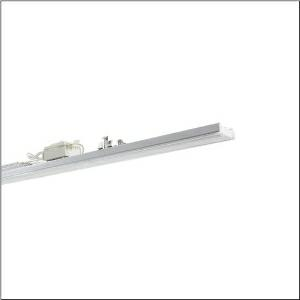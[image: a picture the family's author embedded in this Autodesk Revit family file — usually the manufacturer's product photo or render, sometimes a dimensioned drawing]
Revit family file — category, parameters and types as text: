
# Revit family: licross_r__21_recessed_mo_52tl12dv4fxg_13e3
name_source: partatom
category: Lighting Fixtures
units: mm (PartAtom-declared; Revit-internal decimal feet)

## family parameters
Cut with Voids When Loaded = No
Host = Face
Light Source = No
Part Type = Normal
Room Calculation Point = No
Round Connector Dimension = Use Diameter
Shared = No

## types (1)
- --- (1 x LED, 15420 lm, 85.3 W, 4000K)
    Apparent Load = 85 VA
    CIE Flux Codes = 72 92 99 100 100
    Color Rendering = 80
    Color Temperature = 4000K
    Default Elevation = 1800 mm
    Description = Licross® 21 Recessed MO, luminaire insert, of sheet steel, galvanised, coil coated, white, length: 2.250mm, width: 66mm, height: 67mm, LED rated luminous flux: 15.420lm, light colour: 840, control gear: DALI 2, with plug, 5-pole, with phase selection, mains connection: 220..240V, AC, 50/60Hz, rated input power: 85W, halogen-free wiring, primary optical cover: cover, of PMMA, light emission: direct distribution, primary light characteristic: symmetric, protection rating (complete): IP40, insulation class (complete): insulation class I (protective earthing), certification: CE, ENEC, VDE, UKCA, protection symbol: D if used in an environment without relevant dust loads with corresponding accessories, impact resistance: IK06, permissible ambient temperature for indoor applications: -25..+35°C, corresponds to IFS (International Featured Standards) requirements for safety and quality in the food industry, reducing of maximum allowable ambient temperature of 5°C with ceiling mounting, LABS conformity tested according to VDMA 24364:2018-05, packaging unit: 1 piece
    Height = 58 mm
    Lamp = 1 x LED
    Lamp Light Flux = 15420 lm
    Lamp Power = 85.3 W
    Lamp count = 1
    Length = 2250 mm
    Luminous efficacy = 181 lm/W
    Manufacturer = Siteco
    ModVariant = No
    Model = 52TL12DV4FXG
    Mounting Place = Ceiling
    Mounting Type = Pendant
    Number of Poles = 1
    OnlyDefault = Yes
    Power Factor = 1
    Product Name = Licross® 21 Recessed MO
    Product group = luminaire insert
    ProductGroupID = 902
    Protection Class = Protection class I
    Protection Degree = IP 40
    RLX_Detail_Level = 1
    RLX_Emergency_Light_Flux = 0 lm
    RLX_Emergency_Type = 0
    RLX_Emergency_Type_DB = No
    RlxData = <blob elided: 29313 chars, md5=9abb9c56>
    Socket = socket
    Standby Power = 0 W
    System Light Flux = 15420 lm
    System Power = 85 W
    Type Comments = factory setting: luminous flux: 100 % | dim-lin: 254 | 390 mA
    Type Image = l_1296930.jpg
    URL = http://relux.com
    VarID = @adj_126496
    Voltage = 0 V
    Weight = 0.00 kg
    Width = 66 mm

## geometry (parser evidence)
native form markers: Blend x4, Sweep x10
no freeform markers — native parametric forms only
